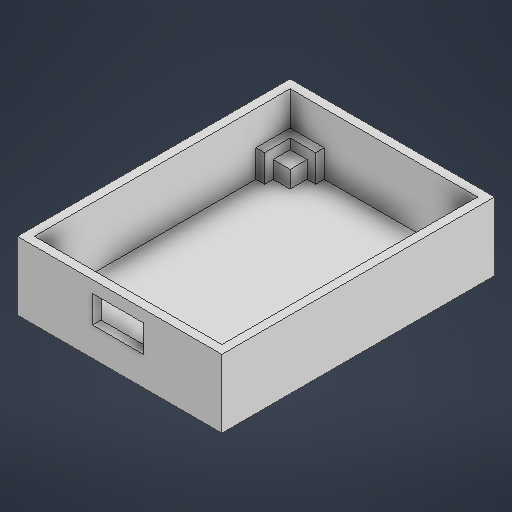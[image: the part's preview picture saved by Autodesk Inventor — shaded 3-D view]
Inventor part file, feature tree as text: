
AUTODESK INVENTOR PART (.ipt)
format: ipt  version: 2025 (Build 290162010, 162A)  size: 299,520 bytes
history: native  units: mm
features: extrude x8, sketch x3
ambient origin geometry x8: Origin, YZ Plane, XZ Plane, XY Plane, X Axis, Y Axis, Z Axis, Center Point
bodies: Solid1 (feature_tree)
feature tree (11):
  sketch  "Sketch1"  dims[d1=55.0mm d2=75.0mm]
  extrude  "Extrusion1"  Depth=75.0mm
  extrude  "Extrusion2"  Depth=60.0mm
  extrude  "Extrusion3"  Depth=2.0mm TaperAngle=0.0deg
  extrude  "Extrusion4"  Depth=7.0mm TaperAngle=0.0deg
  sketch  "Sketch3"  dims[d36=5.0mm d37=2.0mm d38=0.0mm d39=7.0mm d40=0.0mm d41=20.0mm d42=0.0mm d43=1.5mm d52=10.0mm d53=0.0mm d71=8.0mm d72=0.0mm d73=8.0mm d74=0.0mm d75=8.0mm d76=0.0mm d77=8.0mm d78=0.0mm d23=0.5mm d24=0.872665mm d25=0.5mm d26=0.872665mm]
  extrude  "Extrusion5"  Depth=20.0mm TaperAngle=0.0deg
  extrude  "Extrusion6"  Depth=1.5mm
  extrude  "Extrusion7"  Depth=10.0mm TaperAngle=0.0deg
  extrude  "Extrusion8"  Depth=8.0mm TaperAngle=0.0deg
  sketch  "Sketch2"  dims[d34=80.0mm d35=60.0mm]
